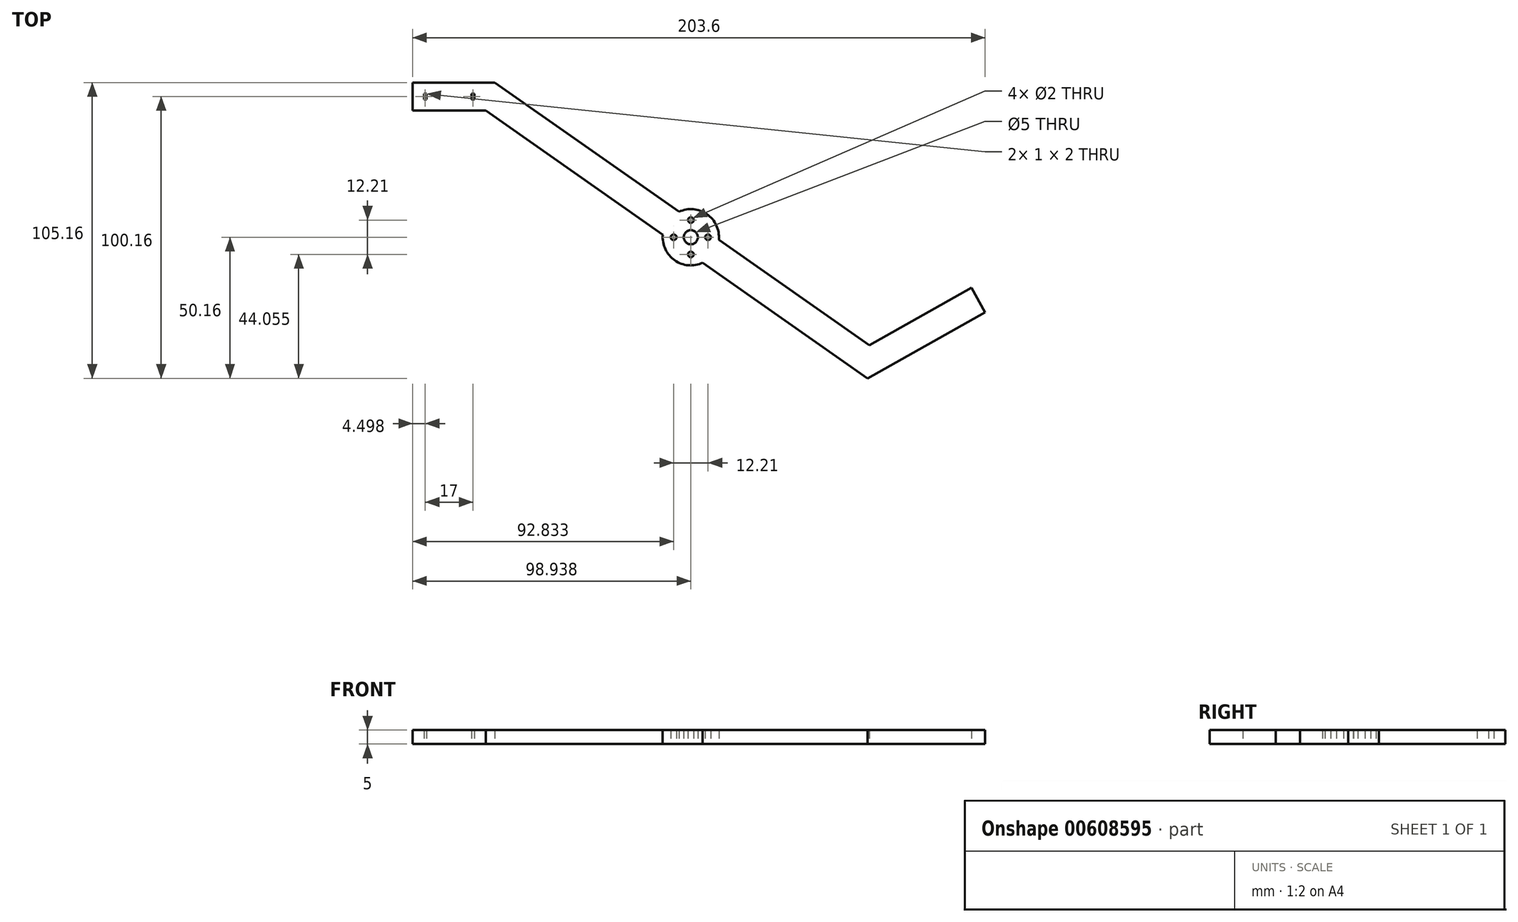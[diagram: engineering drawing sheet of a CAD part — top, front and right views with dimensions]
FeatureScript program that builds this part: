
annotation { "Feature Type Name" : "Feature", "Feature Type Description" : "" }
export const myFeature = defineFeature(function(context is Context, id is Id, definition is map)
    precondition{}
    {
        {
            var Q0;
            Q0=qCreatedBy(makeId("Top.planeOp"),FACE);
            var sketch = newSketch(context, id + "F0", { "sketchPlane" : qUnion([Q0])});
            skCircle(sketch, "E0", {"center": v(0, 0) * mm, "radius": 32.5 * mm, "construction": true});
            skLineSegment(sketch, "E1", {"start": v(0, 0) * mm, "end": v(-189.92, 0) * mm, "construction": true});
            skLineSegment(sketch, "E2", {"start": v(-116.48, 41.92) * mm, "end": v(-69.58, 9.06) * mm});
            skLineSegment(sketch, "E3", {"start": v(-1.9, -38.35) * mm, "end": v(34.4, -17.94) * mm});
            skLineSegment(sketch, "E4.MirrorCS", {"start": v(-1.9, 38.35) * mm, "end": v(34.4, 17.94) * mm, "construction": true});
            skLineSegment(sketch, "E5.MirrorCS", {"start": v(-116.48, -41.92) * mm, "end": v(-1.9, 38.35) * mm, "construction": true});
            skLineSegment(sketch, "E6.MirrorCS", {"start": v(-135.14, 55) * mm, "end": v(-69.58, 9.06) * mm});
            skLineSegment(sketch, "E7.0", {"start": v(-2.51, -50.16) * mm, "end": v(39.3, -26.66) * mm});
            skLineSegment(sketch, "E7.1", {"start": v(-138.3, 45) * mm, "end": v(-75.31, 0.87) * mm});
            skLineSegment(sketch, "E8", {"start": v(34.4, -17.94) * mm, "end": v(39.3, -26.66) * mm});
            skLineSegment(sketch, "E9.0", {"start": v(-2.49, 50.15) * mm, "end": v(39.3, 26.66) * mm, "construction": true});
            skLineSegment(sketch, "E9.1", {"start": v(-138.3, -45) * mm, "end": v(-2.49, 50.15) * mm, "construction": true});
            skLineSegment(sketch, "E10", {"start": v(-65.35, -6.1) * mm, "end": v(-65.35, 6.1) * mm, "construction": true});
            skLineSegment(sketch, "E11", {"start": v(-138.3, 45) * mm, "end": v(-164.3, 45) * mm});
            skLineSegment(sketch, "E12", {"start": v(-164.3, 45) * mm, "end": v(-164.3, 55) * mm});
            skLineSegment(sketch, "E13", {"start": v(-164.3, 55) * mm, "end": v(-135.14, 55) * mm});
            skPoint(sketch, "E14.orphan", {"position": v(-116.48, 41.92) * mm});
            skCircle(sketch, "E15", {"center": v(-65.35, 0) * mm, "radius": 2.5 * mm});
            skCircle(sketch, "E16", {"center": v(-65.35, 0) * mm, "radius": 10 * mm});
            skLineSegment(sketch, "E17.trimOffspring", {"start": v(-55.4, -0.87) * mm, "end": v(-1.9, -38.35) * mm});
            skLineSegment(sketch, "E18.trimOffspring", {"start": v(-61.14, -9.07) * mm, "end": v(-2.51, -50.16) * mm});
            skLineSegment(sketch, "E19", {"start": v(-164.3, 50) * mm, "end": v(-138.3, 50) * mm, "construction": true});
            skLineSegment(sketch, "E20", {"start": v(-151.3, 50) * mm, "end": v(-151.3, 45) * mm, "construction": true});
            skCircle(sketch, "E21", {"center": v(-151.3, 50) * mm, "radius": 8 * mm, "construction": true});
            skLineSegment(sketch, "E22.bottom", {"start": v(-160.3, 51) * mm, "end": v(-159.3, 51) * mm});
            skLineSegment(sketch, "E22.top", {"start": v(-160.3, 49) * mm, "end": v(-159.3, 49) * mm});
            skLineSegment(sketch, "E22.left", {"start": v(-160.3, 51) * mm, "end": v(-160.3, 49) * mm});
            skLineSegment(sketch, "E22.right", {"start": v(-159.3, 51) * mm, "end": v(-159.3, 49) * mm});
            skLineSegment(sketch, "E23.MirrorCS", {"start": v(-142.3, 51) * mm, "end": v(-142.3, 49) * mm});
            skLineSegment(sketch, "E24.MirrorCS", {"start": v(-143.3, 51) * mm, "end": v(-143.3, 49) * mm});
            skLineSegment(sketch, "E25.MirrorCS", {"start": v(-142.3, 49) * mm, "end": v(-143.3, 49) * mm});
            skLineSegment(sketch, "E26.MirrorCS", {"start": v(-142.3, 51) * mm, "end": v(-143.3, 51) * mm});
            skLineSegment(sketch, "E27", {"start": v(-160.3, 50) * mm, "end": v(-159.3, 50) * mm, "construction": true});
            skCircle(sketch, "E28", {"center": v(-65.35, 6.1) * mm, "radius": 1 * mm});
            skCircle(sketch, "E29", {"center": v(-65.35, 0) * mm, "radius": 6.1 * mm, "construction": true});
            skCircle(sketch, "E30.1.0", {"center": v(-71.46, 0) * mm, "radius": 1 * mm});
            skCircle(sketch, "E30.2.0", {"center": v(-65.35, -6.1) * mm, "radius": 1 * mm});
            skCircle(sketch, "E30.3.0", {"center": v(-59.25, 0) * mm, "radius": 1 * mm});
            skSolve(sketch);
        }
        {
            var Q0;
            Q0 = qSketchRegion(id + "F0", true);
            extrude(context, id + "F1", {"entities" : qUnion([Q0]), "depth" : 5 * mm, "offsetDistance" : 25 * mm});
        }
    });
